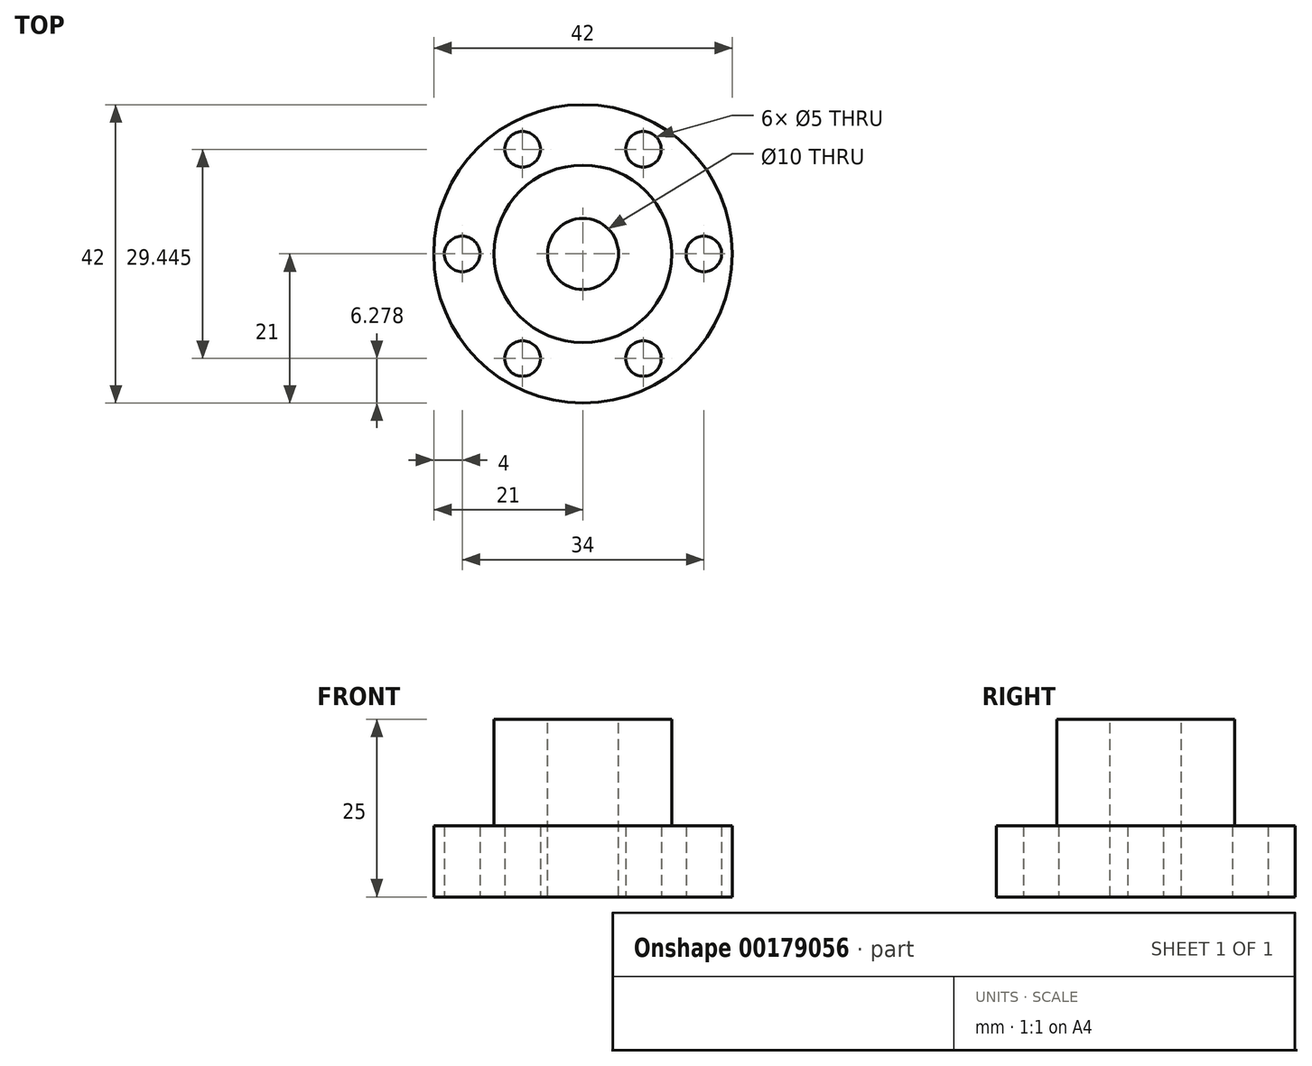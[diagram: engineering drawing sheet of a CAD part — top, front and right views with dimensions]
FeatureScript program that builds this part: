
annotation { "Feature Type Name" : "Feature", "Feature Type Description" : "" }
export const myFeature = defineFeature(function(context is Context, id is Id, definition is map)
    precondition{}
    {
        {
            var Q0;
            Q0=qCreatedBy(makeId("Top.planeOp"),FACE);
            var sketch = newSketch(context, id + "F0", { "sketchPlane" : qUnion([Q0])});
            skCircle(sketch, "E0", {"center": v(0, 0) * mm, "radius": 21 * mm});
            skSolve(sketch);
        }
        {
            var Q0;
            Q0 = qSketchRegion(id + "F0", true);
            extrude(context, id + "F1", {"entities" : qUnion([Q0]), "depth" : 10 * mm});
        }
        {
            var Q0;
            Q0=makeQuery(id+"F1.opExtrude","CAP_FACE",FACE,{"disambiguationData":[OSD([sQuery(id+"F0.wireOp",EDGE,"E0")])],"isStart":false});
            var sketch = newSketch(context, id + "F2", { "sketchPlane" : qUnion([Q0])});
            skCircle(sketch, "E1", {"center": v(0, 0) * mm, "radius": 12.5 * mm});
            skSolve(sketch);
        }
        {
            var Q0;
            Q0 = qSketchRegion(id + "F2", true);
            extrude(context, id + "F3", {"entities" : qUnion([Q0]), "operationType" : NewBodyOperationType.ADD, "depth" : 15 * mm});
        }
        {
            var Q0;
            Q0=makeQuery(id+"F3.opExtrude","CAP_FACE",FACE,{"disambiguationData":[OSD([sQuery(id+"F2.wireOp",EDGE,"E1")])],"isStart":false});
            var sketch = newSketch(context, id + "F4", { "sketchPlane" : qUnion([Q0])});
            skCircle(sketch, "E2", {"center": v(0, 0) * mm, "radius": 5 * mm});
            skSolve(sketch);
        }
        {
            var Q0;
            Q0 = qSketchRegion(id + "F4", true);
            extrude(context, id + "F5", {"entities" : qUnion([Q0]), "operationType" : NewBodyOperationType.REMOVE, "oppositeDirection" : true, "depth" : 30 * mm});
        }
        {
            var Q0;
            Q0=makeQuery(id+"F1.opExtrude","CAP_FACE",FACE,{"disambiguationData":[OSD([sQuery(id+"F0.wireOp",EDGE,"E0")])],"isStart":true});
            var sketch = newSketch(context, id + "F6", { "sketchPlane" : qUnion([Q0])});
            skLineSegment(sketch, "E3", {"start": v(0, 0) * mm, "end": v(38.5, 0) * mm, "construction": true});
            skCircle(sketch, "E4", {"center": v(17, 0) * mm, "radius": 2.5 * mm});
            skCircle(sketch, "E5.1.0", {"center": v(8.5, 14.72) * mm, "radius": 2.5 * mm});
            skCircle(sketch, "E5.2.0", {"center": v(-8.5, 14.72) * mm, "radius": 2.5 * mm});
            skCircle(sketch, "E5.3.0", {"center": v(-17, 0) * mm, "radius": 2.5 * mm});
            skCircle(sketch, "E5.4.0", {"center": v(-8.5, -14.72) * mm, "radius": 2.5 * mm});
            skCircle(sketch, "E5.5.0", {"center": v(8.5, -14.72) * mm, "radius": 2.5 * mm});
            skPoint(sketch, "E5.center", {"position": v(0, 0) * mm});
            skSolve(sketch);
        }
        {
            var Q0;
            Q0 = qSketchRegion(id + "F6", true);
            extrude(context, id + "F7", {"entities" : qUnion([Q0]), "operationType" : NewBodyOperationType.REMOVE, "oppositeDirection" : true, "depth" : 25 * mm});
        }
    });
